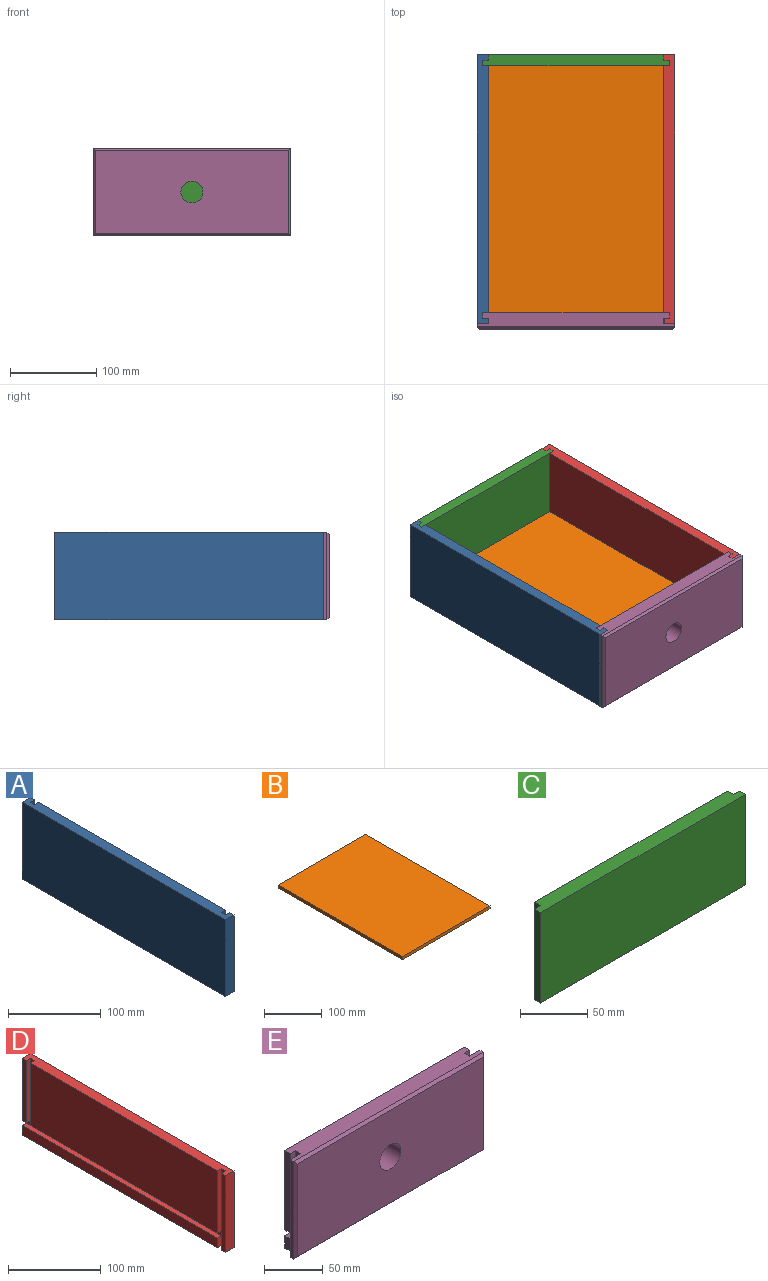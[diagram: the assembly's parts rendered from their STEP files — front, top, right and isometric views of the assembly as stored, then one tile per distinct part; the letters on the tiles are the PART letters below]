
ASSEMBLY  parts=5 mates=4
PART A: 18 faces, bbox 12.7x311.2x101.6 mm
  f0: plane 12.7x6.35mm, normal (0,-1,0), area 80.6mm2, adj f6,f10,f13,f15
  f1: plane 285.75x82.55mm, normal (1,0,0), area 23588.7mm2, adj f5,f8,f12,f16
  f2: plane 82.55x6.35mm, normal (1,0,0), area 524.2mm2, adj f3,f4,f8,f17
  f3: plane 101.6x12.7mm, normal (0,1,0), area 1250mm2, adj f2,f6,f8,f10,f11,f13,f15,f17
  f4: plane 82.55x6.35mm, normal (0,-1,0), area 524.2mm2, adj f2,f8,f13,f17
  f5: plane 82.55x6.35mm, normal (0,1,0), area 524.2mm2, adj f1,f8,f13,f16
  f6: plane 298.45x12.7mm, normal (1,0,0), area 3790.3mm2, adj f0,f3,f10,f15
  f7: plane 101.6x6.35mm, normal (1,0,0), area 645.2mm2, adj f8,f9,f10,f14
  f8: plane 311.15x12.7mm, normal (0,0,1), area 3871mm2, adj f1,f2,f3,f4,f5,f7,f9,f11
  f9: plane 101.6x12.7mm, normal (0,-1,0), area 1290.3mm2, adj f7,f8,f10,f11
  f10: plane 311.15x12.7mm, normal (0,0,-1), area 3911.3mm2, adj f0,f3,f6,f7,f9,f11,f13,f14
  f11: plane 311.15x101.6mm, normal (-1,0,0), area 31612.8mm2, adj f3,f8,f9,f10
  f12: plane 82.55x6.35mm, normal (0,-1,0), area 524.2mm2, adj f1,f8,f13,f16
  f13: plane 304.8x101.6mm, normal (1,0,0), area 3064.5mm2, adj f0,f3,f4,f5,f8,f10,f12,f14
  f14: plane 101.6x6.35mm, normal (0,1,0), area 645.2mm2, adj f7,f8,f10,f13
  f15: plane 298.45x6.35mm, normal (0,0,1), area 1895.2mm2, adj f0,f3,f6,f13
  f16: plane 285.75x6.35mm, normal (0,0,-1), area 1814.5mm2, adj f1,f5,f12,f13
  f17: plane 6.35x6.35mm, normal (0,0,-1), area 40.3mm2, adj f2,f3,f4,f13
PART B: 6 faces, bbox 215.9x304.8x6.4 mm
  f0: plane 215.9x6.35mm, normal (0,-1,0), area 1371mm2, adj f1,f3,f4,f5
  f1: plane 304.8x6.35mm, normal (1,0,0), area 1935.5mm2, adj f0,f2,f4,f5
  f2: plane 215.9x6.35mm, normal (0,1,0), area 1371mm2, adj f1,f3,f4,f5
  f3: plane 304.8x6.35mm, normal (-1,0,0), area 1935.5mm2, adj f0,f2,f4,f5
  f4: plane 304.8x215.9mm, normal (0,0,1), area 65806.3mm2, adj f0,f1,f2,f3
  f5: plane 304.8x215.9mm, normal (0,0,-1), area 65806.3mm2, adj f0,f1,f2,f3
PART C: 10 faces, bbox 215.9x12.7x82.6 mm
  f0: plane 215.9x12.7mm, normal (0,0,-1), area 2661.3mm2, adj f1,f2,f4,f5,f6,f7,f8,f9
  f1: plane 203.2x82.55mm, normal (0,1,0), area 16774.2mm2, adj f0,f3,f6,f8
  f2: plane 82.55x6.35mm, normal (1,0,0), area 524.2mm2, adj f0,f3,f5,f9
  f3: plane 215.9x12.7mm, normal (0,0,1), area 2661.3mm2, adj f1,f2,f4,f5,f6,f7,f8,f9
  f4: plane 82.55x6.35mm, normal (-1,0,0), area 524.2mm2, adj f0,f3,f5,f7
  f5: plane 215.9x82.55mm, normal (0,-1,0), area 17822.5mm2, adj f0,f2,f3,f4
  f6: plane 82.55x6.35mm, normal (-1,0,0), area 524.2mm2, adj f0,f1,f3,f7
  f7: plane 82.55x6.35mm, normal (0,1,0), area 524.2mm2, adj f0,f3,f4,f6
  f8: plane 82.55x6.35mm, normal (1,0,0), area 524.2mm2, adj f0,f1,f3,f9
  f9: plane 82.55x6.35mm, normal (0,1,0), area 524.2mm2, adj f0,f2,f3,f8
PART D: 18 faces, bbox 12.7x311.2x101.6 mm
  f0: plane 285.75x82.55mm, normal (-1,0,0), area 23588.7mm2, adj f3,f6,f14,f17
  f1: plane 6.35x6.35mm, normal (0,0,-1), area 40.3mm2, adj f2,f4,f12,f16
  f2: plane 82.55x6.35mm, normal (-1,0,0), area 524.2mm2, adj f1,f4,f6,f16
  f3: plane 82.55x6.35mm, normal (0,-1,0), area 524.2mm2, adj f0,f6,f12,f14
  f4: plane 101.6x12.7mm, normal (0,1,0), area 1250mm2, adj f1,f2,f6,f8,f9,f10,f12,f15
  f5: plane 101.6x6.35mm, normal (-1,0,0), area 645.2mm2, adj f6,f7,f8,f11
  f6: plane 311.15x12.7mm, normal (0,0,1), area 3871mm2, adj f0,f2,f3,f4,f5,f7,f9,f11
  f7: plane 101.6x12.7mm, normal (0,-1,0), area 1290.3mm2, adj f5,f6,f8,f9
  f8: plane 311.15x12.7mm, normal (0,0,-1), area 3911.3mm2, adj f4,f5,f7,f9,f10,f11,f12,f13
  f9: plane 311.15x101.6mm, normal (1,0,0), area 31612.8mm2, adj f4,f6,f7,f8
  f10: plane 298.45x12.7mm, normal (-1,0,0), area 3790.3mm2, adj f4,f8,f13,f15
  f11: plane 101.6x6.35mm, normal (0,1,0), area 645.2mm2, adj f5,f6,f8,f12
  f12: plane 304.8x101.6mm, normal (-1,0,0), area 3064.5mm2, adj f1,f3,f4,f6,f8,f11,f13,f14
  f13: plane 12.7x6.35mm, normal (0,-1,0), area 80.6mm2, adj f8,f10,f12,f15
  f14: plane 285.75x6.35mm, normal (0,0,-1), area 1814.5mm2, adj f0,f3,f12,f17
  f15: plane 298.45x6.35mm, normal (0,0,1), area 1895.2mm2, adj f4,f10,f12,f13
  f16: plane 82.55x6.35mm, normal (0,-1,0), area 524.2mm2, adj f1,f2,f6,f12
  f17: plane 82.55x6.35mm, normal (0,1,0), area 524.2mm2, adj f0,f6,f12,f14
PART E: 27 faces, bbox 228.6x19.1x101.6 mm
  f0: plane 216.32x12.7mm, normal (0,1,0), area 2747.2mm2, adj f1,f3,f9,f26
  f1: plane 12.7x6.35mm, normal (-1,0,0), area 80.6mm2, adj f0,f2,f9,f26
  f2: plane 12.7x6.35mm, normal (0,-1,0), area 80.6mm2, adj f1,f9,f18,f26
  f3: plane 12.7x6.35mm, normal (1,0,0), area 80.6mm2, adj f0,f9,f21,f26
  f4: plane 82.55x6.35mm, normal (0,-1,0), area 524.2mm2, adj f8,f20,f22,f25
  f5: plane 101.6x3.81mm, normal (1,0,0), area 387.1mm2, adj f8,f9,f11,f23
  f6: plane 101.6x3.81mm, normal (-1,0,0), area 387.1mm2, adj f8,f9,f14,f17
  f7: plane 216.32x82.55mm, normal (0,1,0), area 17350.3mm2, adj f8,f15,f16,f20,f25
  f8: plane 228.6x16.51mm, normal (0,0,1), area 3537.6mm2, adj f4,f5,f6,f7,f12,f16,f17,f18
  f9: plane 228.6x16.51mm, normal (0,0,-1), area 3537.6mm2, adj f0,f1,f2,f3,f5,f6,f13,f17
  f10: plane 223.52x96.52mm, normal (0,-1,0), area 21067.4mm2, adj f11,f12,f13,f14,f15
  f11: plane 101.6x2.54mm, normal (0.71,-0.71,0), area 355.8mm2, adj f5,f10,f12,f13
  f12: plane 228.6x2.54mm, normal (0,-0.71,0.71), area 812mm2, adj f8,f10,f11,f14
  f13: plane 228.6x2.54mm, normal (0,-0.71,-0.71), area 812mm2, adj f9,f10,f11,f14
  f14: plane 101.6x2.54mm, normal (-0.71,-0.71,0), area 355.8mm2, adj f6,f10,f12,f13
  f15: cylinder r=12.7mm len=25.4mm, axis (0,-1,0), area 1520.1mm2, adj f7,f10
  f16: plane 82.55x6.35mm, normal (-1,0,0), area 524.2mm2, adj f7,f8,f19,f25
  f17: plane 101.6x12.66mm, normal (0,1,0), area 1286.6mm2, adj f6,f8,f9,f18
  f18: plane 101.6x6.35mm, normal (-1,0,0), area 645.2mm2, adj f2,f8,f9,f17,f19,f24
  f19: plane 82.55x6.35mm, normal (0,-1,0), area 524.2mm2, adj f8,f16,f18,f25
  f20: plane 82.55x6.35mm, normal (1,0,0), area 524.2mm2, adj f4,f7,f8,f25
  f21: plane 12.7x6.35mm, normal (0,-1,0), area 80.6mm2, adj f3,f9,f22,f26
  f22: plane 101.6x6.35mm, normal (1,0,0), area 645.2mm2, adj f4,f8,f9,f21,f23,f24
  f23: plane 101.6x12.32mm, normal (0,1,0), area 1251.6mm2, adj f5,f8,f9,f22
  f24: plane 203.62x6.35mm, normal (0,1,0), area 1293mm2, adj f18,f22,f25,f26
  f25: plane 216.32x6.35mm, normal (0,0,-1), area 1373.6mm2, adj f4,f7,f16,f19,f20,f24
  f26: plane 216.32x6.35mm, normal (0,0,1), area 1373.6mm2, adj f0,f1,f2,f3,f21,f24
PLACE A t=(-87.08,0.35,-14.26)mm
PLACE B t=(20.86,3.52,-49.19)mm
PLACE C t=(20.87,155.92,-4.74)mm
PLACE D t=(128.82,0.35,-14.26)mm
PLACE E t=(20.68,-152.05,-14.26)mm
MATE fastened B.f0 <-> E.f24  axis (0,-1,0) through (20.86,-148.88,-49.19)mm
MATE fastened D.f7 <-> E.f23  axis (0,-1,0) through (128.82,-155.23,-14.26)mm
MATE fastened C.f2 <-> D.f12  axis (1,0,0) through (128.82,146.4,36.54)mm
MATE fastened A.f13 <-> C.f4  axis (1,0,0) through (-87.08,146.4,36.54)mm
